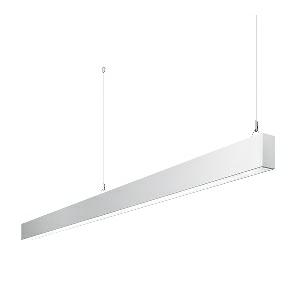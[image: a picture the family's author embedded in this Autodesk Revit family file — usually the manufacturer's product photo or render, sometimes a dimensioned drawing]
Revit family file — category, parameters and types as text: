
# Revit family: dotoo_line_-_dlp_3000_840_d_end_00805787_de6d
name_source: partatom
category: Lighting Fixtures
units: mm (PartAtom-declared; Revit-internal decimal feet)

## family parameters
Cut with Voids When Loaded = No
Host = Face
Light Source = No
Part Type = Normal
Room Calculation Point = No
Round Connector Dimension = Use Diameter
Shared = No

## types (1)
- DOTOO.line - DLP 3000/840/D END (1 x LED, 2750 lm, 4000K)
    Apparent Load = 26 VA
    Approval mark = CE
    CIE Flux Codes = 67 91 98 100 100
    Color Rendering = 80-89
    Color Temperature = 4000K
    Control Gear = Electronic ballast
    Default Elevation = 1800 mm
    Description = DLP 3000/840/D|Suspended luminaire|light source: LED|connected load: 220-240 V, 50/60 Hz|Power consumption: approx. 26 W|standby: approx. 0,15|luminous flux: 2750 lm|luminous efficacy: 105 lm/W|light distribution: Direct|direct ratio: approx. 100 %|colour temperature: Cold white, ca. 4000 K|color rendering index (CRI): >= 80|chromaticity tolerance:  3 SDCM|System of protection: IP 40|technology: Continuously dimmable|luminaire body|material: Sectional aluminium|colour: White|lamp cover: Acrylic (PMMA), Clear|mains lead: 1,0 m With free stranded wires|Fastening: Steel cable 0.3 - 0.7 m|glare control: Prism aperture|luminance(L65): <= 3000 cd/m|unified glare rating(4H 8H): <=  19|special features: DALI Load 1x, TouchDIM - dimming via standard switch, Through-wired, up to 18 m on one mains connection, Flicker-free, Suitable as emergency lighting, Mechanical and electrical connection of the individual modules without tools|
    Frequency = 50 Hz
    Height = 110 mm
    Lamp = 1 x LED
    Lamp Light Flux = 2750 lm
    Lamp count = 1
    Length = 2250 mm
    Luminous efficacy = 106 lm/W
    Manufacturer = Waldmann
    ModVariant = No
    Model = 00805787
    Mounting Place = Ceiling
    Mounting Type = Pendant
    Number of Poles = 1
    OnlyDefault = Yes
    Power Factor = 1
    Product Name = DOTOO.line - DLP 3000/840/D END
    Product group = Suspended luminaire
    ProductGroupID = 9
    Protection Class = Protection class I
    Protection Degree = IP 40
    RLX_Detail_Level = 1
    RLX_Emergency_Light_Flux = 0 lm
    RLX_Emergency_Type = 0
    RLX_Emergency_Type_DB = No
    RlxData = <blob elided: 21045 chars, md5=736a93e5>
    Socket = socket
    Standby Power = 0 W
    System Light Flux = 2750 lm
    System Power = 26 W
    Type Comments = Product without accessories
    Type Image = 113315000-00692609.jpg
    URL = http://relux.com
    VarID = ---
    Voltage = 230 V
    Voltage Range = 220-240 V
    Weight = 0.00 kg
    Width = 60 mm  [stored 0.19685 ft]

note: [stored X ft] marks values corroborated as IEEE doubles in the binary element streams (Revit-internal decimal feet)

## geometry (parser evidence)
native form markers: Blend x4, Sweep x10
no freeform markers — native parametric forms only
